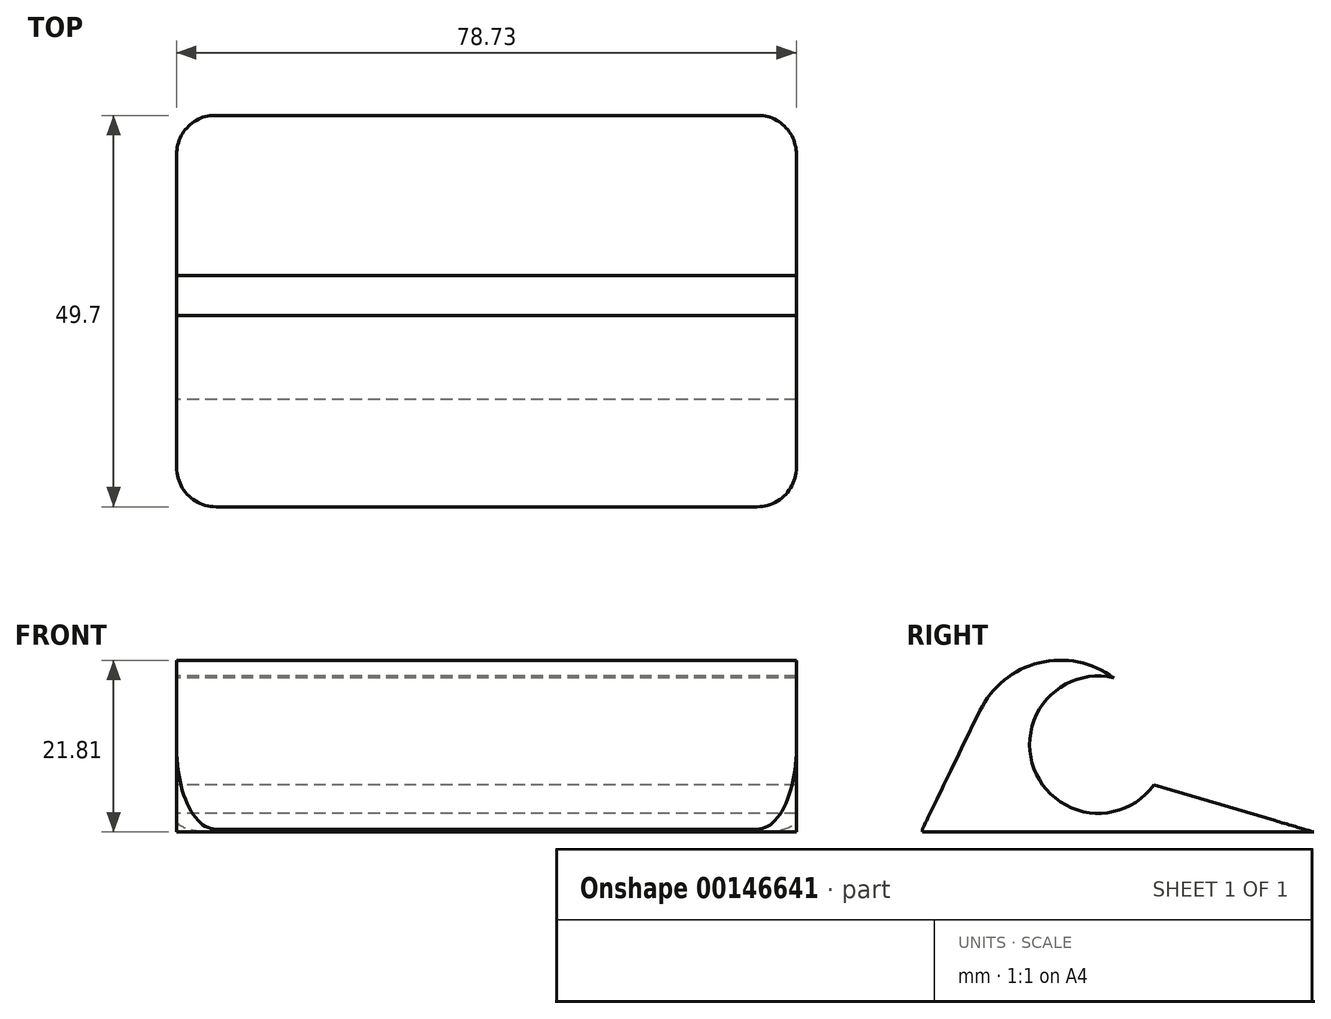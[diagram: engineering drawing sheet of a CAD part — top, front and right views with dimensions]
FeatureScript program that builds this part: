
annotation { "Feature Type Name" : "Feature", "Feature Type Description" : "" }
export const myFeature = defineFeature(function(context is Context, id is Id, definition is map)
    precondition{}
    {
        {
            var Q0;
            Q0=qCreatedBy(makeId("Top.planeOp"),FACE);
            var sketch = newSketch(context, id + "F0", { "sketchPlane" : qUnion([Q0])});
            skLineSegment(sketch, "E0.bottom", {"start": v(-34.5, 33.67) * mm, "end": v(34.24, 33.67) * mm});
            skLineSegment(sketch, "E0.top", {"start": v(-34.5, -16.1) * mm, "end": v(34.24, -16.1) * mm});
            skLineSegment(sketch, "E0.left", {"start": v(-39.5, 28.67) * mm, "end": v(-39.5, -11.1) * mm});
            skLineSegment(sketch, "E0.right", {"start": v(39.24, 28.67) * mm, "end": v(39.24, -11.1) * mm});
            skPoint(sketch, "E1.visualSharp", {"position": v(-39.5, 33.67) * mm});
            skArc(sketch, "E1.filletArc", {"start": v(-34.5, 33.67) * mm, "mid": v(-38.03, 32.2) * mm, "end": v(-39.5, 28.67) * mm});
            skPoint(sketch, "E2.visualSharp", {"position": v(39.24, 33.67) * mm});
            skArc(sketch, "E2.filletArc", {"start": v(39.24, 28.67) * mm, "mid": v(37.78, 32.2) * mm, "end": v(34.24, 33.67) * mm});
            skPoint(sketch, "E3.visualSharp", {"position": v(39.24, -16.1) * mm});
            skArc(sketch, "E3.filletArc", {"start": v(34.24, -16.1) * mm, "mid": v(37.78, -14.63) * mm, "end": v(39.24, -11.1) * mm});
            skPoint(sketch, "E4.visualSharp", {"position": v(-39.5, -16.1) * mm});
            skArc(sketch, "E4.filletArc", {"start": v(-39.5, -11.1) * mm, "mid": v(-38.03, -14.63) * mm, "end": v(-34.5, -16.1) * mm});
            skSolve(sketch);
        }
        {
            var Q0;
            Q0=qSketchRegion(id+"F0",true);
            extrude(context, id + "F1", {"entities" : qUnion([Q0]), "depth" : 36.5 * mm});
        }
        {
            var Q0;
            Q0=makeQuery(id+"F1.opExtrude","SWEPT_FACE",FACE,{"disambiguationData":[OSD([sQuery(id+"F0.wireOp",EDGE,"E0.right")])]});
            var sketch = newSketch(context, id + "F2", { "sketchPlane" : qUnion([Q0])});
            skArc(sketch, "E5", {"start": v(8.21, 19.6) * mm, "mid": v(-1.9, 8.04) * mm, "end": v(13.31, 5.96) * mm});
            skArc(sketch, "E6", {"start": v(8.21, 19.6) * mm, "mid": v(-1.26, 21.48) * mm, "end": v(-8.76, 15.4) * mm});
            skLineSegment(sketch, "E7", {"start": v(-27.4, -11.95) * mm, "end": v(-31.45, 39.27) * mm});
            skLineSegment(sketch, "E8", {"start": v(-31.45, 39.27) * mm, "end": v(12.58, 41.87) * mm});
            skLineSegment(sketch, "E9", {"start": v(12.58, 41.87) * mm, "end": v(53.18, 35.42) * mm});
            skLineSegment(sketch, "E10", {"start": v(53.18, 35.42) * mm, "end": v(54.33, -9.87) * mm});
            skLineSegment(sketch, "E11", {"start": v(54.33, -9.87) * mm, "end": v(33.61, 0) * mm});
            skLineSegment(sketch, "E12", {"start": v(33.61, 0) * mm, "end": v(13.31, 5.96) * mm});
            skLineSegment(sketch, "E13", {"start": v(-27.4, -11.95) * mm, "end": v(-16.25, 0) * mm});
            skLineSegment(sketch, "E14", {"start": v(-16.25, 0) * mm, "end": v(-8.76, 15.4) * mm});
            skSolve(sketch);
        }
        {
            var Q0;
            Q0=qSketchRegion(id+"F2",true);
            extrude(context, id + "F3", {"entities" : qUnion([Q0]), "operationType" : NewBodyOperationType.REMOVE, "depth" : 100 * mm, "hasSecondDirection" : true, "secondDirectionOppositeDirection" : true, "secondDirectionDepth" : 100 * mm});
        }
    });
